# Revit family: BUILDMAT-Ceramic_Pop_Up_Waste
name_source: partatom
category: Plumbing Fixtures
units: mm (PartAtom-declared; Revit-internal decimal feet)

## family parameters
Always vertical = Yes
Cut with Voids When Loaded = Yes
Enable Cutting in Views = Yes
Maintain Annotation Orientation = No
Part Type = Normal
Room Calculation Point = No
Round Connector Dimension = Use Diameter
Shared = No
Work Plane-Based = Yes

## types (8) — shared parameters
Default Elevation = 1219 mm
Depth = 70 mm  [stored 0.229659 ft]
Lock_Material = BM_BRASS GOLD
MainBody_Material = BM_STAINLESS STEEL
Width = 70 mm  [stored 0.229659 ft]

## per-type parameters (varying)
| type | PopUp_Material |
| MATTE BLACK (POPMBLK) | BM_MATTE BLACK |
| MATTE WHITE (POPMTWHT) | BM_MATTE WHITE |
| MATTE PINK (POPUPINK) | BM_MATTE PINK |
| MATTE GREEN (POPGREEN) | BM_MATTE GREEN |
| MATTE BLUE (POPUBLUE) | BM_MATTE BLUE |
| MATTE ECRU SAND (POPUSAND) | BM_MATTE ECRU SAND |
| MATTE GREY (POPUGREY) | BM_MATTE GREY |
| GLOSS WHITE (POPGLWHT) | BM_GLOSS WHITE |

note: [stored X ft] marks values corroborated as IEEE doubles in the binary element streams (Revit-internal decimal feet)

## geometry (parser evidence)
native form markers: Sweep x1
no freeform markers — native parametric forms only
